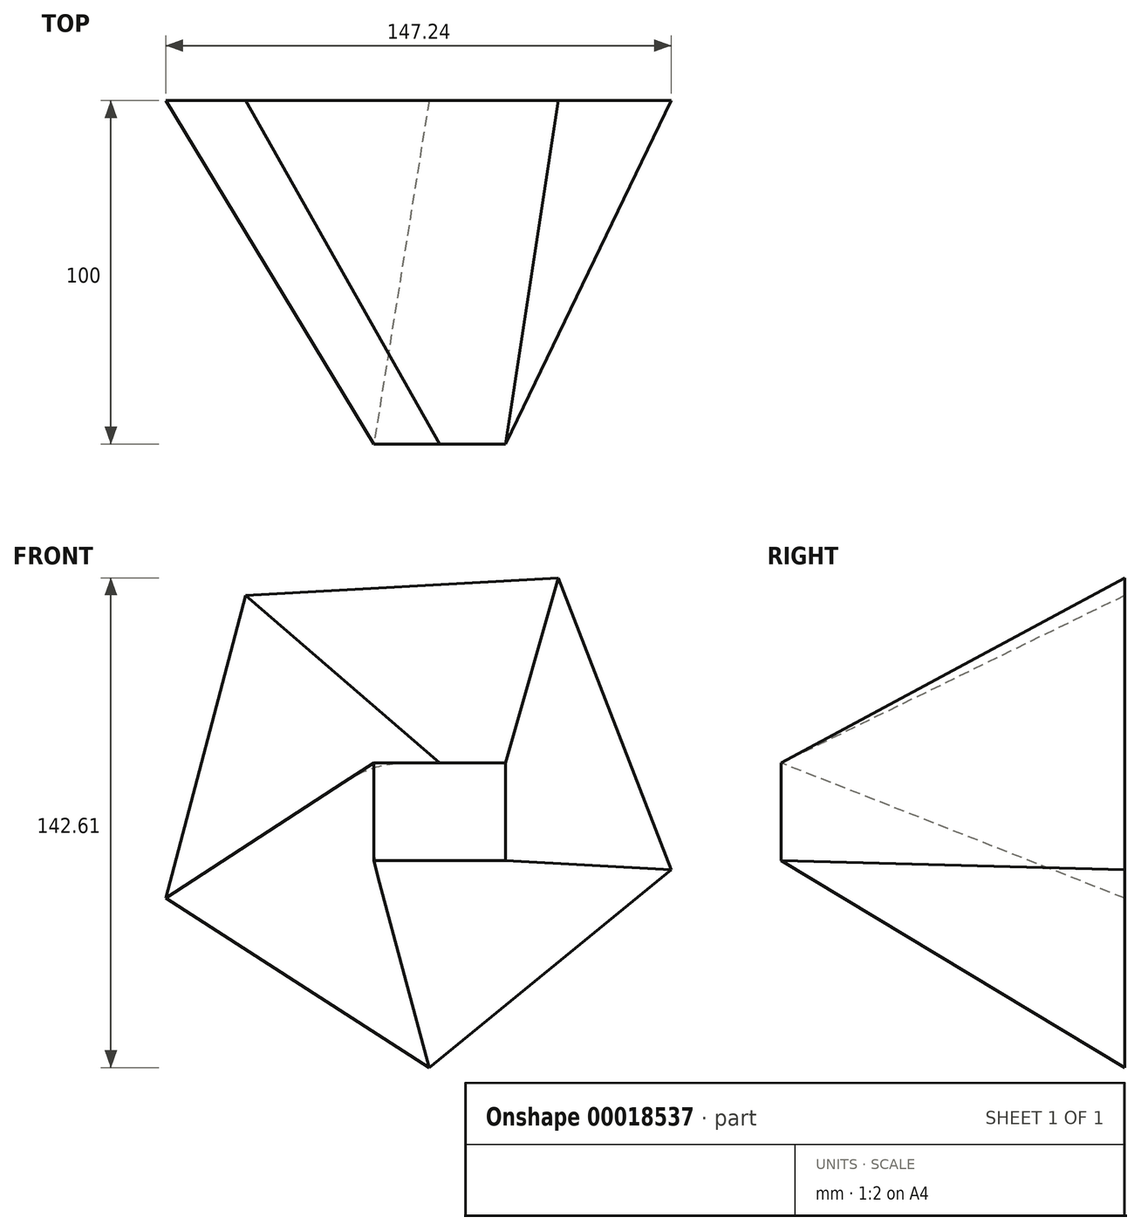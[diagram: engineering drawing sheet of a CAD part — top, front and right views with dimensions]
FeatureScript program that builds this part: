
annotation { "Feature Type Name" : "Feature", "Feature Type Description" : "" }
export const myFeature = defineFeature(function(context is Context, id is Id, definition is map)
    precondition{}
    {
        {
            var Q0;
            Q0=qCreatedBy(makeId("Front.planeOp"),FACE);
            cPlane(context, id + "F0", {"entities" : qUnion([Q0]), "cplaneType" : CPlaneType.OFFSET, "offset" : 100 * mm, "width" : 150 * mm, "height" : 150 * mm});
        }
        {
            var Q0;
            Q0=qCreatedBy(makeId("Front.planeOp"),FACE);
            var sketch = newSketch(context, id + "F1", { "sketchPlane" : qUnion([Q0])});
            skCircle(sketch, "E0.cCircle", {"center": v(0, 0) * mm, "radius": 62.72 * mm, "construction": true});
            skLineSegment(sketch, "E0.0", {"start": v(74.97, -19.76) * mm, "end": v(4.38, -77.4) * mm});
            skLineSegment(sketch, "E0.1", {"start": v(4.38, -77.4) * mm, "end": v(-72.27, -28.08) * mm});
            skLineSegment(sketch, "E0.2", {"start": v(-72.27, -28.08) * mm, "end": v(-49.04, 60.05) * mm});
            skLineSegment(sketch, "E0.3", {"start": v(-49.04, 60.05) * mm, "end": v(41.96, 65.2) * mm});
            skLineSegment(sketch, "E0.4", {"start": v(41.96, 65.2) * mm, "end": v(74.97, -19.76) * mm});
            skPoint(sketch, "E0.0.midPoint", {"position": v(39.67, -48.58) * mm});
            skSolve(sketch);
        }
        {
            var Q0;
            Q0=qCreatedBy(id+"F0.planeOp",FACE);
            var sketch = newSketch(context, id + "F2", { "sketchPlane" : qUnion([Q0])});
            skLineSegment(sketch, "E1.bottom", {"start": v(-11.72, 11.28) * mm, "end": v(26.66, 11.28) * mm});
            skLineSegment(sketch, "E1.top", {"start": v(-11.72, -17.13) * mm, "end": v(26.66, -17.13) * mm});
            skLineSegment(sketch, "E1.left", {"start": v(-11.72, 11.28) * mm, "end": v(-11.72, -17.13) * mm});
            skLineSegment(sketch, "E1.right", {"start": v(26.66, 11.28) * mm, "end": v(26.66, -17.13) * mm});
            skSolve(sketch);
        }
        {
            var Q0;
            Q0=makeQuery(id+"F1.imprint","IMPRINT",FACE,{"disambiguationData":[TD([[makeQuery(id+"F1.imprint","IMPRINT",EDGE,{"derivedFrom":sQuery(id+"F1.wireOp",EDGE,"E0.0")}),-1.0]])]});
            var Q1;
            Q1=makeQuery(id+"F2.imprint","IMPRINT",FACE,{"disambiguationData":[TD([[makeQuery(id+"F2.imprint","IMPRINT",EDGE,{"derivedFrom":sQuery(id+"F2.wireOp",EDGE,"E1.bottom")}),-1.0]])]});
            loft(context, id + "F3", {"sheetProfilesArray" : [{ "sheetProfileEntities" : qUnion([Q0]) }, { "sheetProfileEntities" : qUnion([Q1]) }]});
        }
    });
